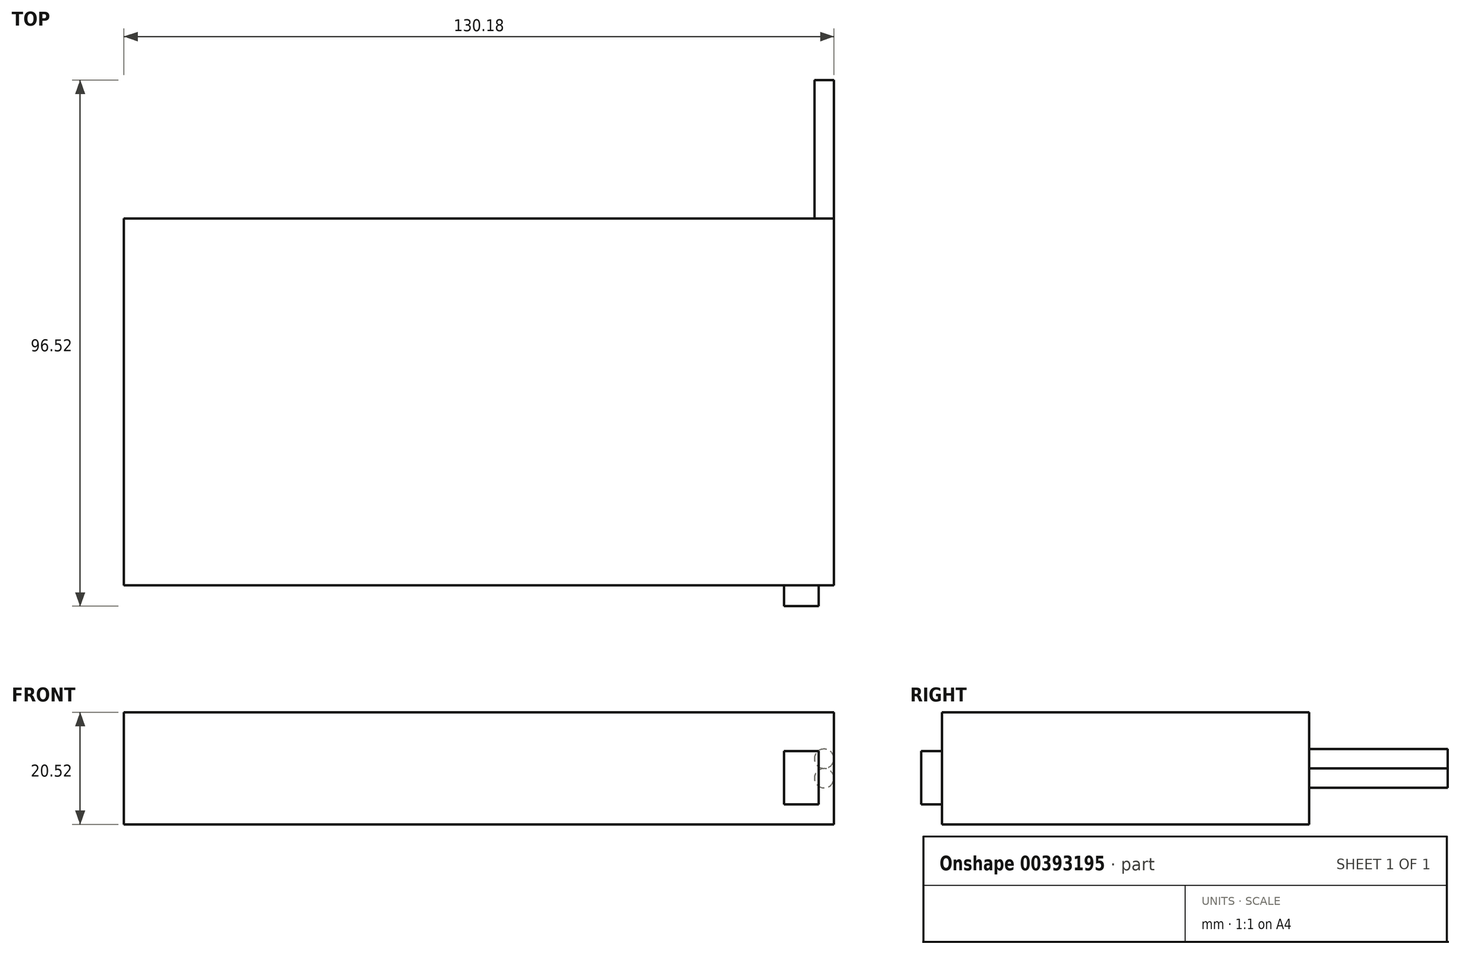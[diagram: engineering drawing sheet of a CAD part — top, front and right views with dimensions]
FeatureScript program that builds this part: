
annotation { "Feature Type Name" : "Feature", "Feature Type Description" : "" }
export const myFeature = defineFeature(function(context is Context, id is Id, definition is map)
    precondition{}
    {
        {
            var Q0;
            Q0=qCreatedBy(makeId("Top.planeOp"),FACE);
            var sketch = newSketch(context, id + "F0", { "sketchPlane" : qUnion([Q0])});
            skLineSegment(sketch, "E0.bottom", {"start": v(0, 0) * mm, "end": v(130.18, 0) * mm});
            skLineSegment(sketch, "E0.top", {"start": v(0, 67.3) * mm, "end": v(130.18, 67.3) * mm});
            skLineSegment(sketch, "E0.left", {"start": v(0, 0) * mm, "end": v(0, 67.3) * mm});
            skLineSegment(sketch, "E0.right", {"start": v(130.18, 0) * mm, "end": v(130.18, 67.3) * mm});
            skSolve(sketch);
        }
        {
            var Q0;
            Q0 = qSketchRegion(id + "F0", true);
            extrude(context, id + "F1", {"entities" : qUnion([Q0]), "depth" : 20.52 * mm});
        }
        {
            var Q0;
            Q0=makeQuery(id+"F1.opExtrude","SWEPT_FACE",FACE,{"disambiguationData":[OSD([sQuery(id+"F0.wireOp",EDGE,"E0.bottom")])]});
            var sketch = newSketch(context, id + "F2", { "sketchPlane" : qUnion([Q0])});
            skLineSegment(sketch, "E1.bottom", {"start": v(121.03, 13.44) * mm, "end": v(127.38, 13.44) * mm});
            skLineSegment(sketch, "E1.top", {"start": v(121.03, 3.66) * mm, "end": v(127.38, 3.66) * mm});
            skLineSegment(sketch, "E1.left", {"start": v(121.03, 13.44) * mm, "end": v(121.03, 3.66) * mm});
            skLineSegment(sketch, "E1.right", {"start": v(127.38, 13.44) * mm, "end": v(127.38, 3.66) * mm});
            skSolve(sketch);
        }
        {
            var Q0;
            Q0 = qSketchRegion(id + "F2", true);
            extrude(context, id + "F3", {"entities" : qUnion([Q0]), "operationType" : NewBodyOperationType.ADD, "depth" : 3.8 * mm});
        }
        {
            var Q0;
            Q0=makeQuery(id+"F1.opExtrude","SWEPT_FACE",FACE,{"disambiguationData":[OSD([sQuery(id+"F0.wireOp",EDGE,"E0.top")])]});
            var sketch = newSketch(context, id + "F4", { "sketchPlane" : qUnion([Q0])});
            skCircle(sketch, "E2", {"center": v(-128.37, 8.46) * mm, "radius": 1.78 * mm});
            skCircle(sketch, "E3", {"center": v(-128.37, 12.04) * mm, "radius": 1.78 * mm});
            skSolve(sketch);
        }
        {
            var Q0;
            Q0 = qSketchRegion(id + "F4", true);
            extrude(context, id + "F5", {"entities" : qUnion([Q0]), "operationType" : NewBodyOperationType.ADD, "depth" : 25.4 * mm});
        }
    });
